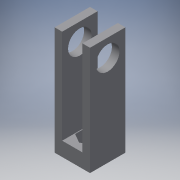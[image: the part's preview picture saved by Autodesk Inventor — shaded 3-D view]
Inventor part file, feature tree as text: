
AUTODESK INVENTOR PART (.ipt)
format: ipt  version: 2016 (Build 200138000, 138)  size: 143,360 bytes
history: native  units: in
note: dims shown in document units (in); Inventor stores cm internally (conversion verified against a paired STEP export)
features: extrude x5, sketch x5
ambient origin geometry x8: Origin, YZ Plane, XZ Plane, XY Plane, X Axis, Y Axis, Z Axis, Center Point
bodies: Solid1 (feature_tree)
feature tree (10):
  extrude  "Extrusion1"  Depth=0.75in
  extrude  "Extrusion2"  Depth=0.4in
  extrude  "Extrusion3"  Depth=0.375in
  extrude  "Extrusion4"  Depth=0.25in
  extrude  "Extrusion5"  Depth=0.75in
  sketch  "Sketch1"  dims[d0=0.75in d1=0.75in]
  sketch  "Sketch2"  dims[d2=0.3in d3=0.0in d4=0.4in]
  sketch  "Sketch3"  dims[d5=0.375in d6=0.375in]
  sketch  "Sketch4"  dims[d7=0.25in d8=0.0in d9=0.19in]
  sketch  "Sketch5"  dims[d10=0.2in d11=0.2in d12=0.5in d13=0.0in d14=0.16in d15=0.16in d16=2.0in d17=0.0in d18=0.5in d19=0.375in d20=0.375in d21=0.75in d22=0.0in]
